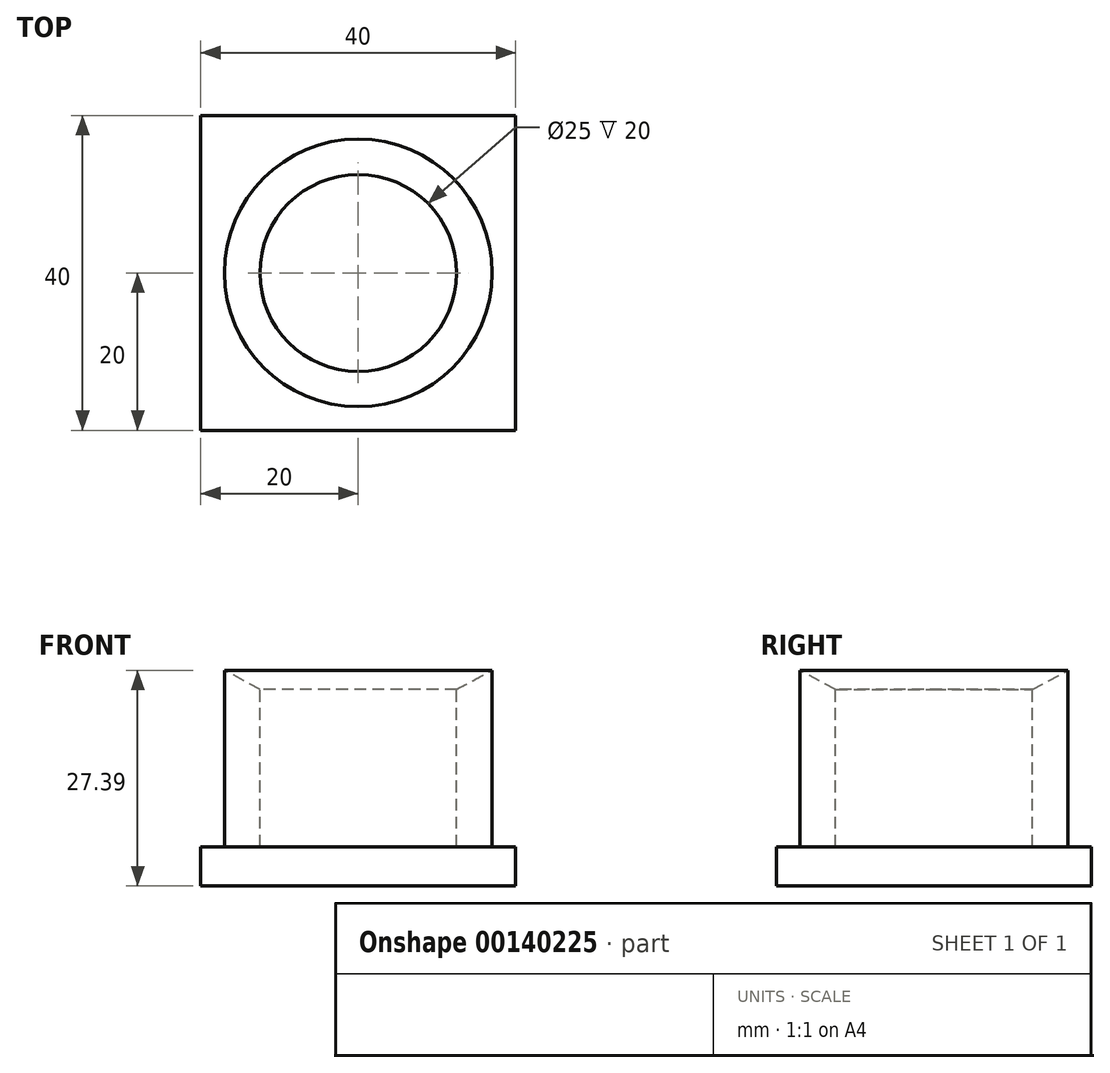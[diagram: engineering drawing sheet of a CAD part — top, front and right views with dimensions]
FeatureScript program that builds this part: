
annotation { "Feature Type Name" : "Feature", "Feature Type Description" : "" }
export const myFeature = defineFeature(function(context is Context, id is Id, definition is map)
    precondition{}
    {
        {
            var Q0;
            Q0=qCreatedBy(makeId("Top.planeOp"),FACE);
            var sketch = newSketch(context, id + "F0", { "sketchPlane" : qUnion([Q0])});
            skLineSegment(sketch, "E0", {"start": v(0, 65.15) * mm, "end": v(0, -74.15) * mm, "construction": true});
            skLineSegment(sketch, "E1", {"start": v(-73.04, 0) * mm, "end": v(85.28, 0) * mm, "construction": true});
            skLineSegment(sketch, "E2.bottom", {"start": v(20, 20) * mm, "end": v(-20, 20) * mm});
            skLineSegment(sketch, "E2.top", {"start": v(20, -20) * mm, "end": v(-20, -20) * mm});
            skLineSegment(sketch, "E2.left", {"start": v(20, 20) * mm, "end": v(20, -20) * mm});
            skLineSegment(sketch, "E2.right", {"start": v(-20, 20) * mm, "end": v(-20, -20) * mm});
            skPoint(sketch, "E2.middle", {"position": v(0, 0) * mm});
            skSolve(sketch);
        }
        {
            var Q0;
            Q0=qSketchRegion(id+"F0",true);
            extrude(context, id + "F1", {"entities" : qUnion([Q0]), "depth" : 5 * mm});
        }
        {
            var Q0;
            Q0=qCreatedBy(makeId("Front.planeOp"),FACE);
            var sketch = newSketch(context, id + "F2", { "sketchPlane" : qUnion([Q0])});
            skLineSegment(sketch, "E3", {"start": v(-33.59, 0) * mm, "end": v(32.44, 0) * mm, "construction": true});
            skLineSegment(sketch, "E4", {"start": v(0, 41.04) * mm, "end": v(0, -5.6) * mm, "construction": true});
            skLineSegment(sketch, "E5.right", {"start": v(-17, 5) * mm, "end": v(-17, 27.4) * mm});
            skLineSegment(sketch, "E6", {"start": v(-17, 27.4) * mm, "end": v(-12.5, 25) * mm});
            skLineSegment(sketch, "E7", {"start": v(-12.5, 25) * mm, "end": v(-12.5, 5) * mm});
            skLineSegment(sketch, "E8", {"start": v(-12.5, 5) * mm, "end": v(-17, 5) * mm});
            skLineSegment(sketch, "E9", {"start": v(-12.5, 25) * mm, "end": v(-17, 25) * mm, "construction": true});
            skSolve(sketch);
        }
        {
            var Q0;
            Q0=qSketchRegion(id+"F2",true);
            var Q1;
            Q1=sQuery(id+"F2.wireOp",EDGE,"E4");
            revolve(context, id + "F3", {"operationType" : NewBodyOperationType.ADD, "entities" : qUnion([Q0]), "axis" : qUnion([Q1]), "revolveType" : RevolveType.FULL});
        }
    });
